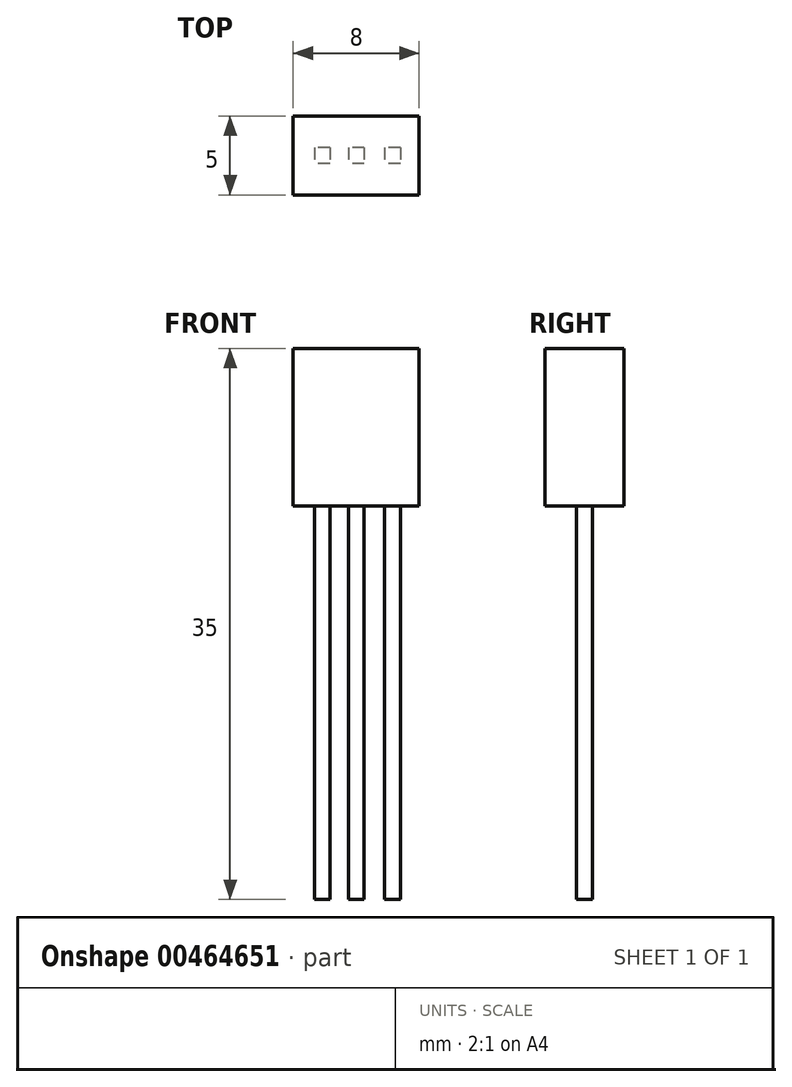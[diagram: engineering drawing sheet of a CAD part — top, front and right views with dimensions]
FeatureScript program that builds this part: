
annotation { "Feature Type Name" : "Feature", "Feature Type Description" : "" }
export const myFeature = defineFeature(function(context is Context, id is Id, definition is map)
    precondition{}
    {
        {
            var Q0;
            Q0=qCreatedBy(makeId("Front.planeOp"),FACE);
            var sketch = newSketch(context, id + "F0", { "sketchPlane" : qUnion([Q0])});
            skLineSegment(sketch, "E0.bottom", {"start": v(-4, 5) * mm, "end": v(4, 5) * mm});
            skLineSegment(sketch, "E0.top", {"start": v(-4, -5) * mm, "end": v(4, -5) * mm});
            skLineSegment(sketch, "E0.left", {"start": v(-4, 5) * mm, "end": v(-4, -5) * mm});
            skLineSegment(sketch, "E0.right", {"start": v(4, 5) * mm, "end": v(4, -5) * mm});
            skPoint(sketch, "E0.middle", {"position": v(0, 0) * mm});
            skSolve(sketch);
        }
        {
            var Q0;
            Q0=makeQuery(id+"F0.imprint","IMPRINT",FACE,{"disambiguationData":[TD([[makeQuery(id+"F0.imprint","IMPRINT",EDGE,{"derivedFrom":sQuery(id+"F0.wireOp",EDGE,"E0.bottom")}),-1.0]])]});
            extrude(context, id + "F1", {"entities" : qUnion([Q0]), "depth" : 5 * mm});
        }
        {
            var Q0;
            Q0=makeQuery(id+"F1.opExtrude","SWEPT_FACE",FACE,{"disambiguationData":[OSD([sQuery(id+"F0.wireOp",EDGE,"E0.top")])]});
            var sketch = newSketch(context, id + "F2", { "sketchPlane" : qUnion([Q0])});
            skPoint(sketch, "E1", {"position": v(-4, 2.5) * mm});
            skLineSegment(sketch, "E2.bottom", {"start": v(0.5, 2) * mm, "end": v(-0.5, 2) * mm});
            skLineSegment(sketch, "E2.top", {"start": v(0.5, 3) * mm, "end": v(-0.5, 3) * mm});
            skLineSegment(sketch, "E2.left", {"start": v(0.5, 2) * mm, "end": v(0.5, 3) * mm});
            skLineSegment(sketch, "E2.right", {"start": v(-0.5, 2) * mm, "end": v(-0.5, 3) * mm});
            skPoint(sketch, "E2.middle", {"position": v(0, 2.5) * mm});
            skLineSegment(sketch, "E3.bottom", {"start": v(2.8, 2) * mm, "end": v(1.8, 2) * mm});
            skLineSegment(sketch, "E3.top", {"start": v(2.8, 3) * mm, "end": v(1.8, 3) * mm});
            skLineSegment(sketch, "E3.left", {"start": v(2.8, 2) * mm, "end": v(2.8, 3) * mm});
            skLineSegment(sketch, "E3.right", {"start": v(1.8, 2) * mm, "end": v(1.8, 3) * mm});
            skPoint(sketch, "E3.middle", {"position": v(2.3, 2.5) * mm});
            skLineSegment(sketch, "E4.bottom", {"start": v(-1.66, 2) * mm, "end": v(-2.66, 2) * mm});
            skLineSegment(sketch, "E4.top", {"start": v(-1.66, 3) * mm, "end": v(-2.66, 3) * mm});
            skLineSegment(sketch, "E4.left", {"start": v(-1.66, 2) * mm, "end": v(-1.66, 3) * mm});
            skLineSegment(sketch, "E4.right", {"start": v(-2.66, 2) * mm, "end": v(-2.66, 3) * mm});
            skPoint(sketch, "E4.middle", {"position": v(-2.16, 2.5) * mm});
            skSolve(sketch);
        }
        {
            var Q0;
            Q0 = qSketchRegion(id + "F2", true);
            extrude(context, id + "F3", {"entities" : qUnion([Q0]), "depth" : 25 * mm});
        }
    });
